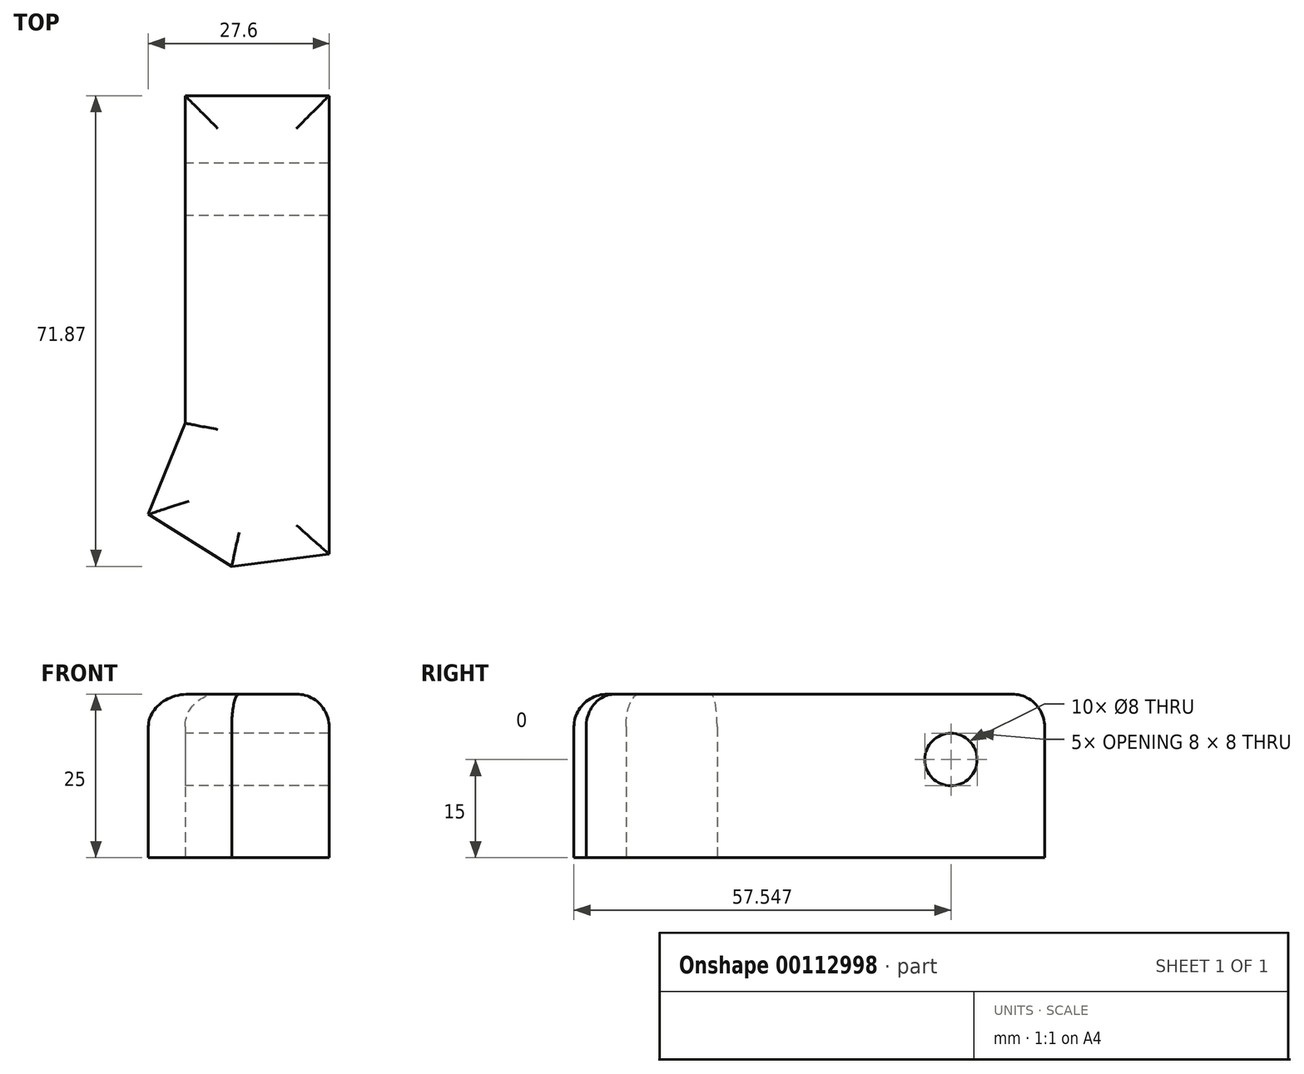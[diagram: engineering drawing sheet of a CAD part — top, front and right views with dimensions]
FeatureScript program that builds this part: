
annotation { "Feature Type Name" : "Feature", "Feature Type Description" : "" }
export const myFeature = defineFeature(function(context is Context, id is Id, definition is map)
    precondition{}
    {
        {
            var Q0;
            Q0=qCreatedBy(makeId("Top.planeOp"),FACE);
            var sketch = newSketch(context, id + "F0", { "sketchPlane" : qUnion([Q0])});
            skLineSegment(sketch, "E0", {"start": v(-17, 47.44) * mm, "end": v(5, 47.44) * mm});
            skLineSegment(sketch, "E1", {"start": v(5, 47.44) * mm, "end": v(5, -22.56) * mm});
            skLineSegment(sketch, "E2", {"start": v(5, -22.56) * mm, "end": v(-9.88, -24.43) * mm});
            skLineSegment(sketch, "E3", {"start": v(-9.88, -24.43) * mm, "end": v(-22.6, -16.48) * mm});
            skLineSegment(sketch, "E4", {"start": v(-22.6, -16.48) * mm, "end": v(-17, -2.56) * mm});
            skLineSegment(sketch, "E5", {"start": v(-17, 47.44) * mm, "end": v(-17, -2.56) * mm});
            skSolve(sketch);
        }
        {
            var Q0;
            Q0=makeQuery(id+"F0.imprint","IMPRINT",FACE,{"disambiguationData":[TD([[makeQuery(id+"F0.imprint","IMPRINT",EDGE,{"derivedFrom":sQuery(id+"F0.wireOp",EDGE,"E0")}),-1.0]])]});
            extrude(context, id + "F1", {"entities" : qUnion([Q0]), "depth" : 25 * mm});
        }
        {
            var Q0;
            Q0=makeQuery(id+"F1.opExtrude","SWEPT_FACE",FACE,{"disambiguationData":[OSD([sQuery(id+"F0.wireOp",EDGE,"E5")])]});
            var sketch = newSketch(context, id + "F2", { "sketchPlane" : qUnion([Q0])});
            skCircle(sketch, "E6", {"center": v(-33.12, 15) * mm, "radius": 4 * mm});
            skSolve(sketch);
        }
        {
            var Q0;
            Q0=makeQuery(id+"F2.imprint","IMPRINT",FACE,{"disambiguationData":[TD([[makeQuery(id+"F2.imprint","IMPRINT",EDGE,{"derivedFrom":sQuery(id+"F2.wireOp",EDGE,"E6")}),1.0]])]});
            extrude(context, id + "F3", {"entities" : qUnion([Q0]), "operationType" : NewBodyOperationType.REMOVE, "endBound" : BoundingType.THROUGH_ALL, "oppositeDirection" : true, "depth" : 25 * mm});
        }
        {
            var Q0;
            Q0=makeQuery(id+"F1.opExtrude","CAP_FACE",FACE,{"disambiguationData":[OSD([sQuery(id+"F0.wireOp",EDGE,"E0"),sQuery(id+"F0.wireOp",EDGE,"E1"),sQuery(id+"F0.wireOp",EDGE,"E2"),sQuery(id+"F0.wireOp",EDGE,"E3"),sQuery(id+"F0.wireOp",EDGE,"E4"),sQuery(id+"F0.wireOp",EDGE,"E5")])],"isStart":false});
            fillet(context, id + "F4", {"entities" : qUnion([Q0]), "radius" : 5 * mm, "tangentPropagation" : true, "allowEdgeOverflow" : false});
        }
    });
